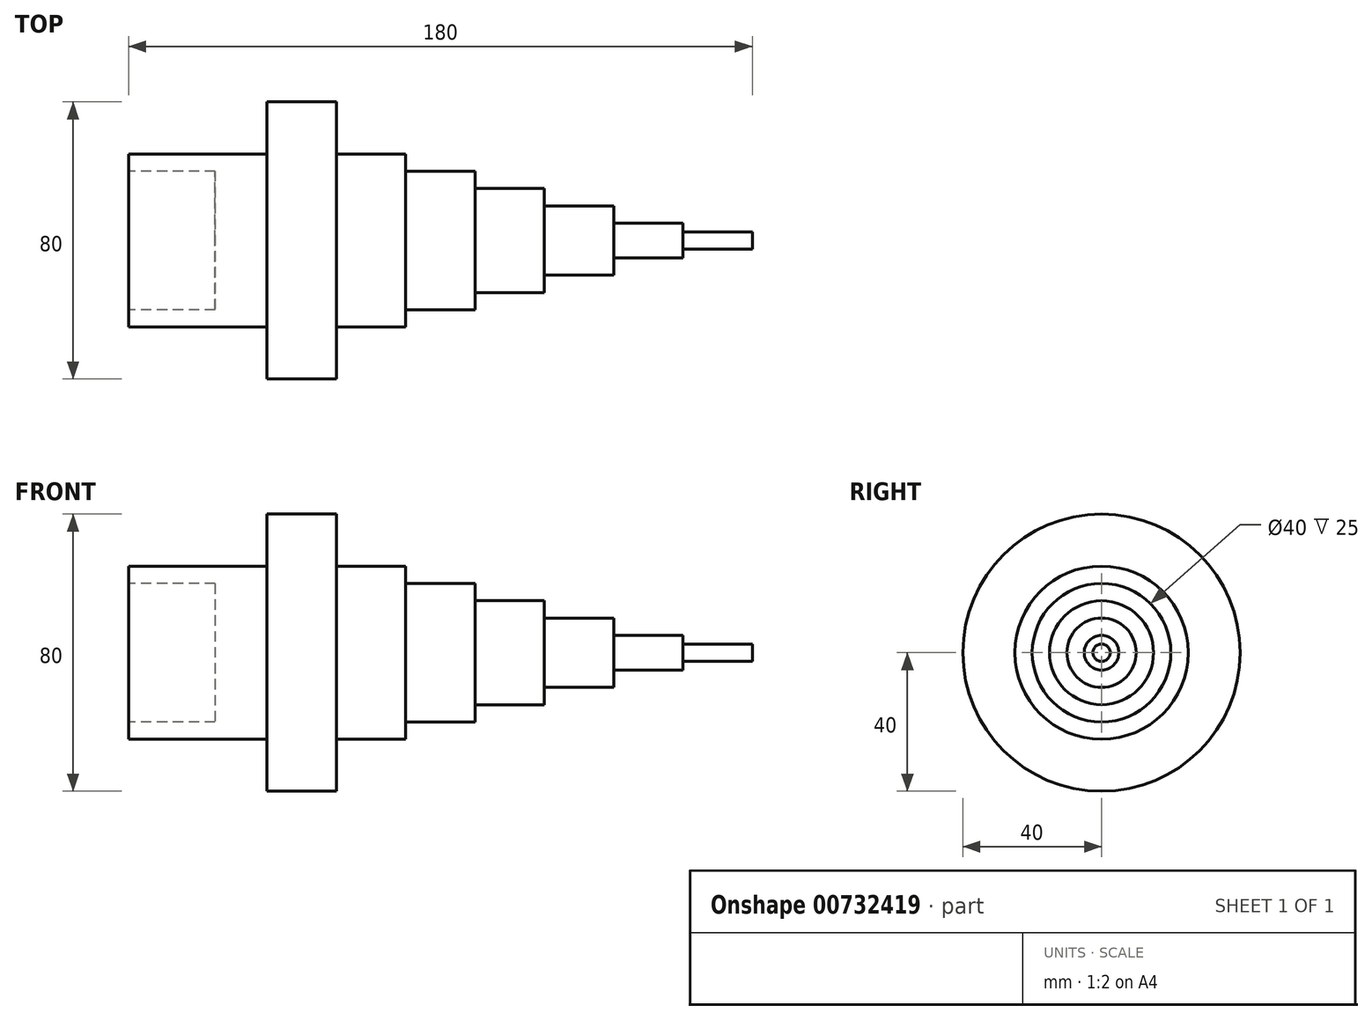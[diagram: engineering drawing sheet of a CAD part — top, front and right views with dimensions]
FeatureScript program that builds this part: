
annotation { "Feature Type Name" : "Feature", "Feature Type Description" : "" }
export const myFeature = defineFeature(function(context is Context, id is Id, definition is map)
    precondition{}
    {
        {
            var Q0;
            Q0=qCreatedBy(makeId("Front.planeOp"),FACE);
            var sketch = newSketch(context, id + "F0", { "sketchPlane" : qUnion([Q0])});
            skLineSegment(sketch, "E0", {"start": v(-374.64, 0) * mm, "end": v(-374.64, 25) * mm});
            skLineSegment(sketch, "E1", {"start": v(-374.64, 25) * mm, "end": v(-334.64, 25) * mm});
            skLineSegment(sketch, "E2", {"start": v(-334.64, 25) * mm, "end": v(-334.64, 40) * mm});
            skLineSegment(sketch, "E3", {"start": v(-334.64, 40) * mm, "end": v(-314.64, 40) * mm});
            skLineSegment(sketch, "E4", {"start": v(-314.64, 40) * mm, "end": v(-314.64, 25) * mm});
            skLineSegment(sketch, "E5", {"start": v(-314.64, 25) * mm, "end": v(-294.64, 25) * mm});
            skLineSegment(sketch, "E6", {"start": v(-294.64, 25) * mm, "end": v(-294.64, 20) * mm});
            skLineSegment(sketch, "E7", {"start": v(-294.64, 20) * mm, "end": v(-274.64, 20) * mm});
            skLineSegment(sketch, "E8", {"start": v(-274.64, 20) * mm, "end": v(-274.64, 15) * mm});
            skLineSegment(sketch, "E9", {"start": v(-274.64, 15) * mm, "end": v(-254.64, 15) * mm});
            skLineSegment(sketch, "E10", {"start": v(-254.64, 15) * mm, "end": v(-254.64, 10) * mm});
            skLineSegment(sketch, "E11", {"start": v(-254.64, 10) * mm, "end": v(-234.64, 10) * mm});
            skLineSegment(sketch, "E12", {"start": v(-234.64, 10) * mm, "end": v(-234.64, 5) * mm});
            skLineSegment(sketch, "E13", {"start": v(-234.64, 5) * mm, "end": v(-214.64, 5) * mm});
            skLineSegment(sketch, "E14", {"start": v(-214.64, 5) * mm, "end": v(-214.64, 2.5) * mm});
            skLineSegment(sketch, "E15", {"start": v(-214.64, 2.5) * mm, "end": v(-194.64, 2.5) * mm});
            skLineSegment(sketch, "E16", {"start": v(-194.64, 2.5) * mm, "end": v(-194.64, 0) * mm});
            skLineSegment(sketch, "E17", {"start": v(-374.64, 0) * mm, "end": v(-194.64, 0) * mm});
            skSolve(sketch);
        }
        {
            var Q0;
            Q0=makeQuery(id+"F0.imprint","IMPRINT",FACE,{"disambiguationData":[TD([[makeQuery(id+"F0.imprint","IMPRINT",EDGE,{"derivedFrom":sQuery(id+"F0.wireOp",EDGE,"E0")}),-1.0]])]});
            var Q1;
            Q1=sQuery(id+"F0.wireOp",EDGE,"E17");
            revolve(context, id + "F1", {"surfaceOperationType" : NewSurfaceOperationType.NEW, "entities" : qUnion([Q0]), "axis" : qUnion([Q1]), "revolveType" : RevolveType.FULL});
        }
        {
            var Q0;
            Q0=makeQuery(id+"F1.opRevolve","SWEPT_FACE",FACE,{"disambiguationData":[OSD([sQuery(id+"F0.wireOp",EDGE,"E0")])]});
            var sketch = newSketch(context, id + "F2", { "sketchPlane" : qUnion([Q0])});
            skCircle(sketch, "E18", {"center": v(0, 0) * mm, "radius": 20 * mm});
            skSolve(sketch);
        }
        {
            var Q0;
            Q0 = qSketchRegion(id + "F2", true);
            extrude(context, id + "F3", {"entities" : qUnion([Q0]), "operationType" : NewBodyOperationType.REMOVE, "oppositeDirection" : true, "depth" : 25 * mm, "offsetDistance" : 25 * mm});
        }
    });
